# Revit family: spectral_stora_stora-qp-led_5200_840_os_1a4a
name_source: partatom
category: Lighting Fixtures
revit_build: Autodesk Revit 2016 (Build: 20150220_1215(x64)
units: mm (PartAtom-declared; Revit-internal decimal feet)

## family parameters
Cut with Voids When Loaded = No
Host = Face
Light Source = No
Part Type = Normal
Room Calculation Point = No
Round Connector Dimension = Use Diameter
Shared = No

## types (1)
- SPECTRAL STORA (1 x )
    Apparent Load = 0 VA
    CIE Flux Codes = 47 78 95 100 72
    Control Gear = Electronic transformer
    Default Elevation = 1800 mm
    Description = SPC0620029
STORA pendant LED luminaire

Design:
Square luminaire element with an opal acrylic panel mounted in a profile 
frame made of power-coated aluminium. The luminaire is suspended by a 
wire pendant with ceiling fixture and transparent connecting cable with rectangular powder-coated ceiling junction box. The cable length can be adjusted at the ceiling junction box, the steel wire can be steplessly height adjusted at the luminaire. At the top of the luminaire, the control gear is accommodated under a cover which can be removed for maintenance using 
a keyhole screw connection. The LED module is formed as a square LED flat board. Luminaire with heatresistant wiring. Homogeneous illumination of the light surface. Light colour 4000 K (840), dimmable. Protection rating IP20, safety class I.

Colour:
Frame – similar to RAL 9016 white silk matt
    Height = 50 mm
    Lamp = 1 x
    Lamp count = 1
    Length = 580 mm
    Luminous efficacy = 0 lm/W
    Manufacturer = Ridi
    ModVariant = No
    Model = STORA-QP-LED 5200/840 OS
    Mounting Place = Ceiling
    Mounting Type = Pendant
    Number of Poles = 1
    OnlyDefault = Yes
    Power Factor = 1
    Product Name = SPECTRAL STORA
    Product group = Pendant luminaire
    ProductGroupID = 9
    Protection Class = Protection class
    Protection Degree = Degree of protection
    RlxData = <blob elided: 13281 chars, md5=1d49d5e4>
    Socket = socket
    Standby Power = 0 W
    System Light Flux = 0 lm
    System Power = 0 W
    Type Image = stora-qp_512.jpg
    URL = http://reluxnet.relux.com
    VarID = 1
    Voltage = 0 V
    Weight = 0.00 kg
    Width = 580 mm

## geometry (parser evidence)
native form markers: Sweep x11
no freeform markers — native parametric forms only
